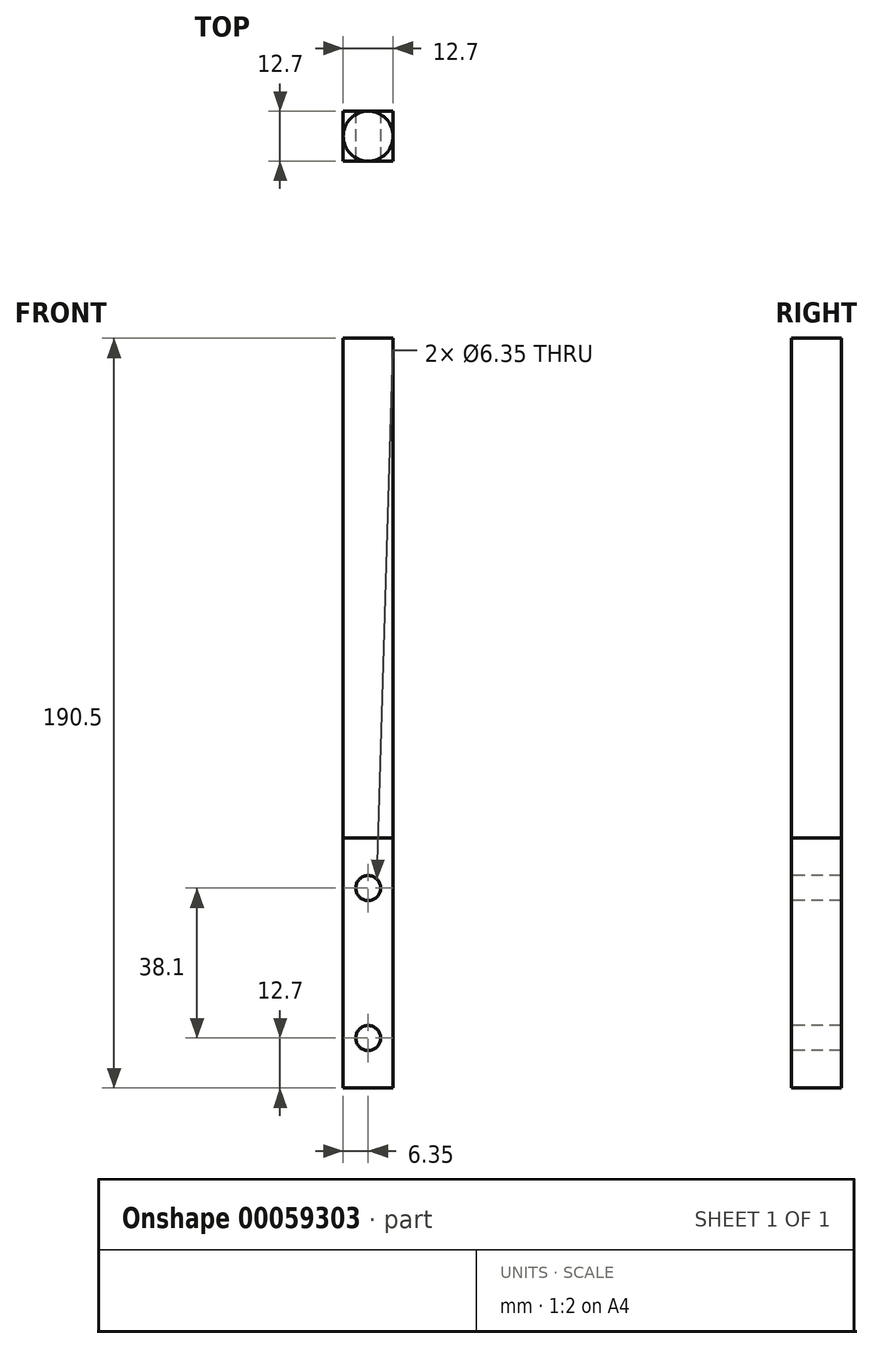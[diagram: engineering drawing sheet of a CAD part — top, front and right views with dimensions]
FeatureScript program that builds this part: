
annotation { "Feature Type Name" : "Feature", "Feature Type Description" : "" }
export const myFeature = defineFeature(function(context is Context, id is Id, definition is map)
    precondition{}
    {
        {
            var Q0;
            Q0=qCreatedBy(makeId("Top.planeOp"),FACE);
            var sketch = newSketch(context, id + "F0", { "sketchPlane" : qUnion([Q0])});
            skCircle(sketch, "E0", {"center": v(0, 0) * mm, "radius": 6.35 * mm});
            skSolve(sketch);
        }
        {
            var Q0;
            Q0=makeQuery(id+"F0.imprint","IMPRINT",FACE,{"disambiguationData":[TD([[makeQuery(id+"F0.imprint","IMPRINT",EDGE,{"derivedFrom":sQuery(id+"F0.wireOp",EDGE,"E0")}),1.0]])]});
            extrude(context, id + "F1", {"entities" : qUnion([Q0]), "depth" : 127 * mm});
        }
        {
            var Q0;
            Q0=makeQuery(id+"F1.opExtrude","CAP_FACE",FACE,{"disambiguationData":[OSD([sQuery(id+"F0.wireOp",EDGE,"E0")])],"isStart":true});
            var sketch = newSketch(context, id + "F2", { "sketchPlane" : qUnion([Q0])});
            skLineSegment(sketch, "E1.bottom", {"start": v(-6.35, 6.35) * mm, "end": v(6.35, 6.35) * mm});
            skLineSegment(sketch, "E1.top", {"start": v(-6.35, -6.35) * mm, "end": v(6.35, -6.35) * mm});
            skLineSegment(sketch, "E1.left", {"start": v(-6.35, 6.35) * mm, "end": v(-6.35, -6.35) * mm});
            skLineSegment(sketch, "E1.right", {"start": v(6.35, 6.35) * mm, "end": v(6.35, -6.35) * mm});
            skSolve(sketch);
        }
        {
            var Q0;
            {var subQ0=sQuery(id+"F2.wireOp",EDGE,"E1.right");var subQ1=sQuery(id+"F2.wireOp",EDGE,"E1.bottom");var subQ2=makeQuery(id+"F2.imprint","INTERSECT",VERTEX,{"derivedFrom":[subQ1,subQ0]});Q0=makeQuery(id+"F2.imprint","IMPRINT",FACE,{"disambiguationData":[TD([[makeQuery(id+"F2.imprint","IMPRINT",EDGE,{"disambiguationData":[TD([[subQ2,1.0]])],"derivedFrom":subQ1}),-1.0]])]});}
            var Q1;
            {var subQ0=sQuery(id+"F2.wireOp",EDGE,"E1.right");var subQ1=sQuery(id+"F2.wireOp",EDGE,"E1.top");var subQ2=makeQuery(id+"F2.imprint","INTERSECT",VERTEX,{"derivedFrom":[subQ1,subQ0]});Q1=makeQuery(id+"F2.imprint","IMPRINT",FACE,{"disambiguationData":[TD([[makeQuery(id+"F2.imprint","IMPRINT",EDGE,{"disambiguationData":[TD([[subQ2,1.0]])],"derivedFrom":subQ1}),1.0]])]});}
            var Q2;
            {var subQ0=makeQuery(id+"F1.opExtrude","CAP_EDGE",EDGE,{"disambiguationData":[OSD([sQuery(id+"F0.wireOp",EDGE,"E0")])],"isStart":true});var subQ1=makeQuery(id+"F2.imprint","INTERSECT",VERTEX,{"derivedFrom":[subQ0,sQuery(id+"F2.wireOp",EDGE,"E1.bottom")]});Q2=makeQuery(id+"F2.imprint","IMPRINT",FACE,{"disambiguationData":[TD([[makeQuery(id+"F2.imprint","IMPRINT",EDGE,{"disambiguationData":[TD([[subQ1,1.0]])],"derivedFrom":subQ0}),-1.0]])]});}
            var Q3;
            {var subQ0=sQuery(id+"F2.wireOp",EDGE,"E1.left");var subQ1=sQuery(id+"F2.wireOp",EDGE,"E1.bottom");var subQ2=makeQuery(id+"F2.imprint","INTERSECT",VERTEX,{"derivedFrom":[subQ1,subQ0]});Q3=makeQuery(id+"F2.imprint","IMPRINT",FACE,{"disambiguationData":[TD([[makeQuery(id+"F2.imprint","IMPRINT",EDGE,{"disambiguationData":[TD([[subQ2,-1.0]])],"derivedFrom":subQ1}),-1.0]])]});}
            var Q4;
            {var subQ0=sQuery(id+"F2.wireOp",EDGE,"E1.left");var subQ1=sQuery(id+"F2.wireOp",EDGE,"E1.top");var subQ2=makeQuery(id+"F2.imprint","INTERSECT",VERTEX,{"derivedFrom":[subQ1,subQ0]});Q4=makeQuery(id+"F2.imprint","IMPRINT",FACE,{"disambiguationData":[TD([[makeQuery(id+"F2.imprint","IMPRINT",EDGE,{"disambiguationData":[TD([[subQ2,-1.0]])],"derivedFrom":subQ1}),1.0]])]});}
            extrude(context, id + "F3", {"entities" : qUnion([Q0, Q1, Q2, Q3, Q4]), "operationType" : NewBodyOperationType.ADD, "depth" : 63.5 * mm});
        }
        {
            var Q0;
            Q0=makeQuery(id+"F3.opExtrude","SWEPT_FACE",FACE,{"disambiguationData":[OSD([sQuery(id+"F2.wireOp",EDGE,"E1.bottom")])]});
            var sketch = newSketch(context, id + "F4", { "sketchPlane" : qUnion([Q0])});
            skCircle(sketch, "E2", {"center": v(0, -12.7) * mm, "radius": 3.18 * mm});
            skCircle(sketch, "E3", {"center": v(0, -50.8) * mm, "radius": 3.18 * mm});
            skSolve(sketch);
        }
        {
            var Q0;
            Q0=sQuery(id+"F4.wireOp",VERTEX,"E2.center");
            var Q1;
            Q1=sQuery(id+"F4.wireOp",VERTEX,"E3.center");
            var Q2;
            Q2=makeQuery(id+"F1.opExtrude","SWEPT_BODY",BODY,{"disambiguationData":[OSD([sQuery(id+"F0.wireOp",EDGE,"E0")])]});
            hole(context, id + "F5", {"style" : HoleStyle.SIMPLE, "holeDiameter" : 6.35 * mm, "endStyle" : HoleEndStyle.THROUGH, "locations" : qUnion([Q0, Q1]), "scope" : qUnion([Q2])});
        }
    });
